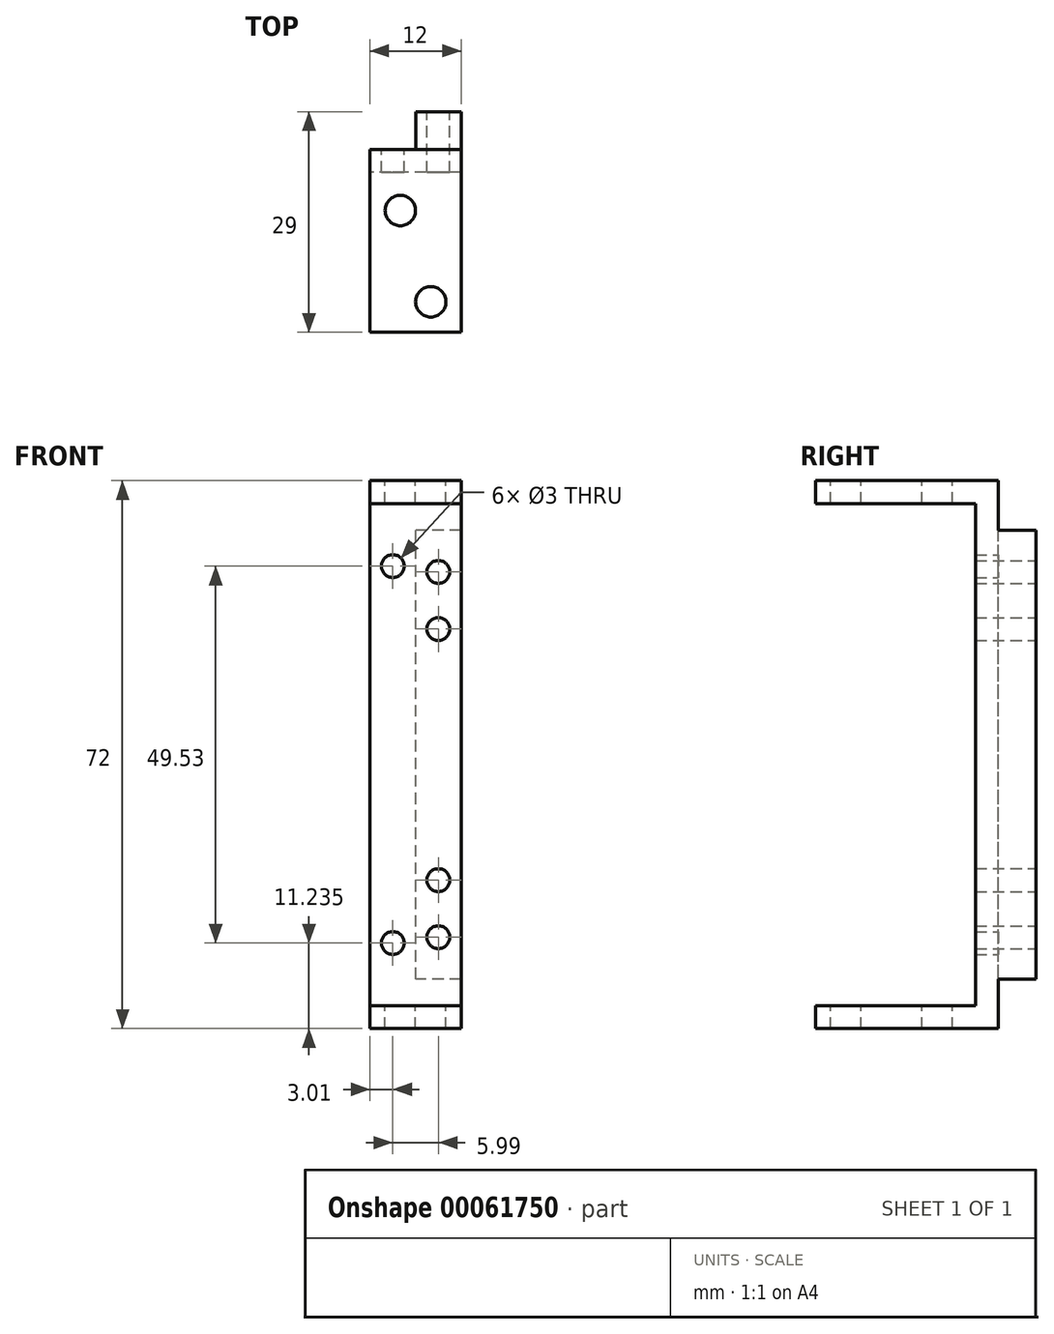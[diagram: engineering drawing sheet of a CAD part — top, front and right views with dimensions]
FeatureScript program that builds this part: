
annotation { "Feature Type Name" : "Feature", "Feature Type Description" : "" }
export const myFeature = defineFeature(function(context is Context, id is Id, definition is map)
    precondition{}
    {
        {
            var Q0;
            Q0=qCreatedBy(makeId("Right.planeOp"),FACE);
            var sketch = newSketch(context, id + "F0", { "sketchPlane" : qUnion([Q0])});
            skLineSegment(sketch, "E0", {"start": v(-10.5, 37.5) * mm, "end": v(18.5, 37.5) * mm});
            skLineSegment(sketch, "E1", {"start": v(18.5, 37.5) * mm, "end": v(18.5, -34.5) * mm});
            skLineSegment(sketch, "E2.0", {"start": v(10.5, 34.5) * mm, "end": v(10.5, -34.5) * mm});
            skLineSegment(sketch, "E2.1", {"start": v(-10.5, 34.5) * mm, "end": v(10.5, 34.5) * mm});
            skLineSegment(sketch, "E3", {"start": v(-10.5, 37.5) * mm, "end": v(-10.5, 34.5) * mm});
            skLineSegment(sketch, "E4", {"start": v(18.5, -34.5) * mm, "end": v(10.5, -34.5) * mm});
            skLineSegment(sketch, "E5", {"start": v(10.5, 0) * mm, "end": v(-14.36, 0) * mm, "construction": true});
            skLineSegment(sketch, "E6", {"start": v(0, 34.5) * mm, "end": v(0, -1.72) * mm, "construction": true});
            skSolve(sketch);
        }
        {
            var Q0;
            Q0=makeQuery(id+"F0.imprint","IMPRINT",FACE,{"disambiguationData":[TD([[makeQuery(id+"F0.imprint","IMPRINT",EDGE,{"derivedFrom":sQuery(id+"F0.wireOp",EDGE,"E0")}),-1.0]])]});
            extrude(context, id + "F1", {"entities" : qUnion([Q0]), "depth" : 12 * mm});
        }
        {
            var Q0;
            Q0=makeQuery(id+"F1.opExtrude","SWEPT_FACE",FACE,{"disambiguationData":[OSD([sQuery(id+"F0.wireOp",EDGE,"E0")])]});
            var sketch = newSketch(context, id + "F2", { "sketchPlane" : qUnion([Q0])});
            skLineSegment(sketch, "E7.bottom", {"start": v(0, 18.5) * mm, "end": v(6.02, 18.5) * mm});
            skLineSegment(sketch, "E7.top", {"start": v(0, 13.5) * mm, "end": v(6.02, 13.5) * mm});
            skLineSegment(sketch, "E7.left", {"start": v(0, 18.5) * mm, "end": v(0, 13.5) * mm});
            skLineSegment(sketch, "E7.right", {"start": v(6.02, 18.5) * mm, "end": v(6.02, 13.5) * mm});
            skSolve(sketch);
        }
        {
            var Q0;
            Q0=makeQuery(id+"F2.imprint","IMPRINT",FACE,{"disambiguationData":[TD([[makeQuery(id+"F2.imprint","IMPRINT",EDGE,{"derivedFrom":sQuery(id+"F2.wireOp",EDGE,"E7.bottom")}),1.0]])]});
            extrude(context, id + "F3", {"entities" : qUnion([Q0]), "operationType" : NewBodyOperationType.REMOVE, "oppositeDirection" : true, "depth" : 72 * mm});
        }
        {
            var Q0;
            Q0=makeQuery(id+"F1.opExtrude","SWEPT_FACE",FACE,{"disambiguationData":[OSD([sQuery(id+"F0.wireOp",EDGE,"E1")])]});
            var sketch = newSketch(context, id + "F4", { "sketchPlane" : qUnion([Q0])});
            skCircle(sketch, "E8", {"center": v(-9, 25.5) * mm, "radius": 1.5 * mm});
            skCircle(sketch, "E9", {"center": v(-9, -22.5) * mm, "radius": 1.5 * mm});
            skLineSegment(sketch, "E10", {"start": v(-9, 25.5) * mm, "end": v(-9, -22.5) * mm, "construction": true});
            skPoint(sketch, "E11", {"position": v(-9, 37.5) * mm});
            skLineSegment(sketch, "E12", {"start": v(-9, 25.5) * mm, "end": v(-9, 37.5) * mm, "construction": true});
            skSolve(sketch);
        }
        {
            var Q0;
            Q0=makeQuery(id+"F4.imprint","IMPRINT",FACE,{"disambiguationData":[TD([[makeQuery(id+"F4.imprint","IMPRINT",EDGE,{"derivedFrom":sQuery(id+"F4.wireOp",EDGE,"E8")}),1.0]])]});
            var Q1;
            Q1=makeQuery(id+"F4.imprint","IMPRINT",FACE,{"disambiguationData":[TD([[makeQuery(id+"F4.imprint","IMPRINT",EDGE,{"derivedFrom":sQuery(id+"F4.wireOp",EDGE,"E9")}),1.0]])]});
            extrude(context, id + "F5", {"entities" : qUnion([Q0, Q1]), "operationType" : NewBodyOperationType.REMOVE, "oppositeDirection" : true, "depth" : 25 * mm});
        }
        {
            var Q0;
            Q0=makeQuery(id+"F3.boolean.opBoolean","COPY",FACE,{"derivedFrom":makeQuery(id+"F3.opExtrude","SWEPT_FACE",FACE,{"disambiguationData":[OSD([sQuery(id+"F2.wireOp",EDGE,"E7.top")])]})});
            var sketch = newSketch(context, id + "F6", { "sketchPlane" : qUnion([Q0])});
            skCircle(sketch, "E13", {"center": v(-3, 26.27) * mm, "radius": 1.5 * mm});
            skCircle(sketch, "E14", {"center": v(-3, -23.27) * mm, "radius": 1.5 * mm});
            skLineSegment(sketch, "E15", {"start": v(-3, 26.27) * mm, "end": v(-3, -23.27) * mm, "construction": true});
            skPoint(sketch, "E16", {"position": v(-3, 37.5) * mm});
            skSolve(sketch);
        }
        {
            var Q0;
            Q0=makeQuery(id+"F6.imprint","IMPRINT",FACE,{"disambiguationData":[TD([[makeQuery(id+"F6.imprint","IMPRINT",EDGE,{"derivedFrom":sQuery(id+"F6.wireOp",EDGE,"E14")}),1.0]])]});
            var Q1;
            Q1=makeQuery(id+"F6.imprint","IMPRINT",FACE,{"disambiguationData":[TD([[makeQuery(id+"F6.imprint","IMPRINT",EDGE,{"derivedFrom":sQuery(id+"F6.wireOp",EDGE,"E13")}),1.0]])]});
            extrude(context, id + "F7", {"entities" : qUnion([Q0, Q1]), "operationType" : NewBodyOperationType.REMOVE, "oppositeDirection" : true, "depth" : 25 * mm});
        }
        {
            var Q0;
            Q0=makeQuery(id+"F1.opExtrude","SWEPT_FACE",FACE,{"disambiguationData":[OSD([sQuery(id+"F0.wireOp",EDGE,"E2.0")])]});
            var sketch = newSketch(context, id + "F8", { "sketchPlane" : qUnion([Q0])});
            skLineSegment(sketch, "E17.bottom", {"start": v(0, -34.5) * mm, "end": v(12, -34.5) * mm});
            skLineSegment(sketch, "E17.top", {"start": v(0, -31.5) * mm, "end": v(12, -31.5) * mm});
            skLineSegment(sketch, "E17.left", {"start": v(0, -31.5) * mm, "end": v(0, -34.5) * mm});
            skLineSegment(sketch, "E17.right", {"start": v(12, -31.5) * mm, "end": v(12, -34.5) * mm});
            skSolve(sketch);
        }
        {
            var Q0;
            Q0=makeQuery(id+"F8.imprint","IMPRINT",FACE,{"disambiguationData":[TD([[makeQuery(id+"F8.imprint","IMPRINT",EDGE,{"derivedFrom":sQuery(id+"F8.wireOp",EDGE,"E17.bottom")}),-1.0]])]});
            extrude(context, id + "F9", {"entities" : qUnion([Q0]), "operationType" : NewBodyOperationType.ADD, "depth" : 21 * mm});
        }
        {
            var Q0;
            Q0=makeQuery(id+"F1.opExtrude","SWEPT_FACE",FACE,{"disambiguationData":[OSD([sQuery(id+"F0.wireOp",EDGE,"E0")])]});
            var sketch = newSketch(context, id + "F10", { "sketchPlane" : qUnion([Q0])});
            skCircle(sketch, "E18", {"center": v(4, 5.5) * mm, "radius": 2 * mm});
            skCircle(sketch, "E19", {"center": v(8, -6.5) * mm, "radius": 2 * mm});
            skSolve(sketch);
        }
        {
            var Q0;
            Q0=makeQuery(id+"F10.imprint","IMPRINT",FACE,{"disambiguationData":[TD([[makeQuery(id+"F10.imprint","IMPRINT",EDGE,{"derivedFrom":sQuery(id+"F10.wireOp",EDGE,"E18")}),1.0]])]});
            var Q1;
            Q1=makeQuery(id+"F10.imprint","IMPRINT",FACE,{"disambiguationData":[TD([[makeQuery(id+"F10.imprint","IMPRINT",EDGE,{"derivedFrom":sQuery(id+"F10.wireOp",EDGE,"E19")}),1.0]])]});
            extrude(context, id + "F11", {"entities" : qUnion([Q0, Q1]), "operationType" : NewBodyOperationType.REMOVE, "oppositeDirection" : true, "depth" : 72 * mm});
        }
        {
            var Q0;
            Q0=makeQuery(id+"F1.opExtrude","SWEPT_FACE",FACE,{"disambiguationData":[OSD([sQuery(id+"F0.wireOp",EDGE,"E1")])]});
            var sketch = newSketch(context, id + "F12", { "sketchPlane" : qUnion([Q0])});
            skLineSegment(sketch, "E20.bottom", {"start": v(-12, 37.5) * mm, "end": v(-6.02, 37.5) * mm});
            skLineSegment(sketch, "E20.top", {"start": v(-12, 31) * mm, "end": v(-6.02, 31) * mm});
            skLineSegment(sketch, "E20.left", {"start": v(-12, 37.5) * mm, "end": v(-12, 31) * mm});
            skLineSegment(sketch, "E20.right", {"start": v(-6.02, 37.5) * mm, "end": v(-6.02, 31) * mm});
            skLineSegment(sketch, "E21.bottom", {"start": v(-12, -34.5) * mm, "end": v(-6.02, -34.5) * mm});
            skLineSegment(sketch, "E21.top", {"start": v(-12, -28) * mm, "end": v(-6.02, -28) * mm});
            skLineSegment(sketch, "E21.left", {"start": v(-12, -34.5) * mm, "end": v(-12, -28) * mm});
            skLineSegment(sketch, "E21.right", {"start": v(-6.02, -34.5) * mm, "end": v(-6.02, -28) * mm});
            skSolve(sketch);
        }
        {
            var Q0;
            Q0 = qSketchRegion(id + "F12", true);
            extrude(context, id + "F13", {"entities" : qUnion([Q0]), "operationType" : NewBodyOperationType.REMOVE, "oppositeDirection" : true, "depth" : 5 * mm});
        }
        {
            var Q0;
            Q0=makeQuery(id+"F1.opExtrude","SWEPT_FACE",FACE,{"disambiguationData":[OSD([sQuery(id+"F0.wireOp",EDGE,"E1")])]});
            var sketch = newSketch(context, id + "F14", { "sketchPlane" : qUnion([Q0])});
            skCircle(sketch, "E22", {"center": v(-9, -15) * mm, "radius": 1.5 * mm});
            skCircle(sketch, "E23", {"center": v(-9, 18) * mm, "radius": 1.5 * mm});
            skLineSegment(sketch, "E24", {"start": v(-9, 18) * mm, "end": v(-9, -15) * mm, "construction": true});
            skSolve(sketch);
        }
        {
            var Q0;
            Q0 = qSketchRegion(id + "F14", true);
            extrude(context, id + "F15", {"entities" : qUnion([Q0]), "operationType" : NewBodyOperationType.REMOVE, "oppositeDirection" : true, "depth" : 25 * mm});
        }
    });
